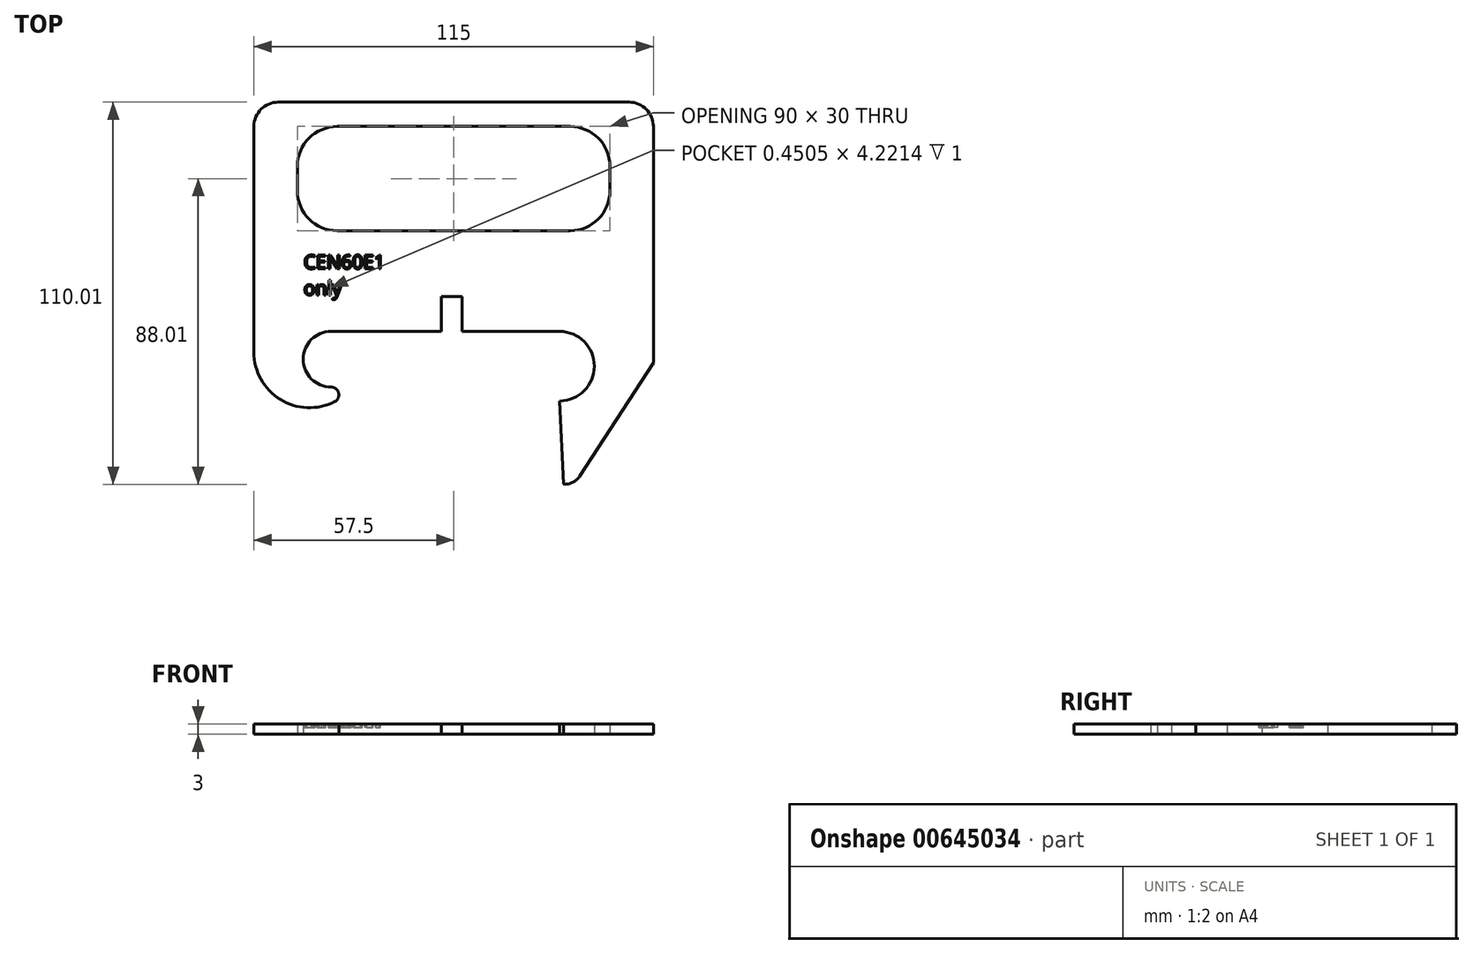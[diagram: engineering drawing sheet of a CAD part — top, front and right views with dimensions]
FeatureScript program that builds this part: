
annotation { "Feature Type Name" : "Feature", "Feature Type Description" : "" }
export const myFeature = defineFeature(function(context is Context, id is Id, definition is map)
    precondition{}
    {
        {
            var Q0;
            Q0=qCreatedBy(makeId("Top.planeOp"),FACE);
            var sketch = newSketch(context, id + "F0", { "sketchPlane" : qUnion([Q0])});
            skLineSegment(sketch, "E0.bottom", {"start": v(100.56, 114.07) * mm, "end": v(-100.56, 114.07) * mm, "construction": true});
            skLineSegment(sketch, "E0.top", {"start": v(100.56, -114.07) * mm, "end": v(-100.56, -114.07) * mm, "construction": true});
            skLineSegment(sketch, "E0.left", {"start": v(100.56, 114.07) * mm, "end": v(100.56, -114.07) * mm, "construction": true});
            skLineSegment(sketch, "E0.right", {"start": v(-100.56, 114.07) * mm, "end": v(-100.56, -114.07) * mm, "construction": true});
            skPoint(sketch, "E0.middle", {"position": v(0, 0) * mm});
            skLineSegment(sketch, "E1", {"start": v(0, 0) * mm, "end": v(-31.71, 0) * mm});
            skLineSegment(sketch, "E2", {"start": v(0, 0) * mm, "end": v(0, 10) * mm});
            skLineSegment(sketch, "E3", {"start": v(0, 10) * mm, "end": v(6, 10) * mm});
            skLineSegment(sketch, "E4", {"start": v(6, 10) * mm, "end": v(6, 0) * mm});
            skLineSegment(sketch, "E5", {"start": v(6, 0) * mm, "end": v(34.08, 0) * mm});
            skArc(sketch, "E6", {"start": v(34.08, -20) * mm, "mid": v(44.08, -10) * mm, "end": v(34.08, 0) * mm});
            skLineSegment(sketch, "E7", {"start": v(34.08, -20) * mm, "end": v(35.28, -44) * mm});
            skLineSegment(sketch, "E8", {"start": v(34.08, -20) * mm, "end": v(34.08, -27.07) * mm, "construction": true});
            skLineSegment(sketch, "E9", {"start": v(61.08, -9) * mm, "end": v(61.08, 59) * mm});
            skLineSegment(sketch, "E10", {"start": v(61.08, -9) * mm, "end": v(39.82, -41.74) * mm});
            skArc(sketch, "E11", {"start": v(39.82, -41.74) * mm, "mid": v(37.86, -43.49) * mm, "end": v(35.28, -44) * mm});
            skArc(sketch, "E12", {"start": v(-31.71, 0) * mm, "mid": v(-39.71, -8) * mm, "end": v(-31.71, -16) * mm});
            skArc(sketch, "E13", {"start": v(-30.7, -20.24) * mm, "mid": v(-29.53, -17.72) * mm, "end": v(-31.71, -16) * mm});
            skArc(sketch, "E14", {"start": v(-30.7, -20.24) * mm, "mid": v(-46.3, -19.6) * mm, "end": v(-53.92, -5.96) * mm});
            skLineSegment(sketch, "E15", {"start": v(-53.92, -5.96) * mm, "end": v(-53.92, 59) * mm});
            skLineSegment(sketch, "E16", {"start": v(54.08, 66) * mm, "end": v(-46.92, 66) * mm});
            skPoint(sketch, "E17.visualSharp", {"position": v(61.08, 66) * mm});
            skArc(sketch, "E17.filletArc", {"start": v(61.08, 59) * mm, "mid": v(59.03, 63.95) * mm, "end": v(54.08, 66) * mm});
            skPoint(sketch, "E18.visualSharp", {"position": v(-53.92, 66) * mm});
            skArc(sketch, "E18.filletArc", {"start": v(-46.92, 66) * mm, "mid": v(-51.87, 63.95) * mm, "end": v(-53.92, 59) * mm});
            skLineSegment(sketch, "E19.bottom", {"start": v(-29.94, 59) * mm, "end": v(37.1, 59) * mm});
            skLineSegment(sketch, "E19.top", {"start": v(-29.94, 29) * mm, "end": v(37.1, 29) * mm});
            skLineSegment(sketch, "E19.left", {"start": v(-41.42, 47.52) * mm, "end": v(-41.42, 40.48) * mm});
            skLineSegment(sketch, "E19.right", {"start": v(48.58, 47.52) * mm, "end": v(48.58, 40.48) * mm});
            skPoint(sketch, "E20.visualSharp", {"position": v(-41.42, 59) * mm});
            skArc(sketch, "E20.filletArc", {"start": v(-29.94, 59) * mm, "mid": v(-38.06, 55.64) * mm, "end": v(-41.42, 47.52) * mm});
            skPoint(sketch, "E21.visualSharp", {"position": v(-41.42, 29) * mm});
            skArc(sketch, "E21.filletArc", {"start": v(-41.42, 40.48) * mm, "mid": v(-38.06, 32.36) * mm, "end": v(-29.94, 29) * mm});
            skPoint(sketch, "E22.visualSharp", {"position": v(48.58, 29) * mm});
            skArc(sketch, "E22.filletArc", {"start": v(37.1, 29) * mm, "mid": v(45.22, 32.36) * mm, "end": v(48.58, 40.48) * mm});
            skPoint(sketch, "E23.visualSharp", {"position": v(48.58, 59) * mm});
            skArc(sketch, "E23.filletArc", {"start": v(48.58, 47.52) * mm, "mid": v(45.22, 55.64) * mm, "end": v(37.1, 59) * mm});
            skSolve(sketch);
        }
        {
            var Q0;
            Q0=makeQuery(id+"F0.imprint","IMPRINT",FACE,{"disambiguationData":[TD([[makeQuery(id+"F0.imprint","IMPRINT",EDGE,{"derivedFrom":sQuery(id+"F0.wireOp",EDGE,"E1")}),-1.0]])]});
            extrude(context, id + "F1", {"entities" : qUnion([Q0]), "depth" : 3 * mm, "offsetDistance" : 25 * mm});
        }
        {
            var Q0;
            Q0=makeQuery(id+"F1.opExtrude","CAP_FACE",FACE,{"disambiguationData":[OSD([sQuery(id+"F0.wireOp",EDGE,"E1"),sQuery(id+"F0.wireOp",EDGE,"E2"),sQuery(id+"F0.wireOp",EDGE,"E3"),sQuery(id+"F0.wireOp",EDGE,"E4"),sQuery(id+"F0.wireOp",EDGE,"E5"),sQuery(id+"F0.wireOp",EDGE,"E6"),sQuery(id+"F0.wireOp",EDGE,"E7"),sQuery(id+"F0.wireOp",EDGE,"E9"),sQuery(id+"F0.wireOp",EDGE,"E10"),sQuery(id+"F0.wireOp",EDGE,"E11"),sQuery(id+"F0.wireOp",EDGE,"E12"),sQuery(id+"F0.wireOp",EDGE,"E13"),sQuery(id+"F0.wireOp",EDGE,"E14"),sQuery(id+"F0.wireOp",EDGE,"E15"),sQuery(id+"F0.wireOp",EDGE,"E16"),sQuery(id+"F0.wireOp",EDGE,"E17.filletArc"),sQuery(id+"F0.wireOp",EDGE,"E18.filletArc"),sQuery(id+"F0.wireOp",EDGE,"E19.bottom"),sQuery(id+"F0.wireOp",EDGE,"E19.top"),sQuery(id+"F0.wireOp",EDGE,"E19.left"),sQuery(id+"F0.wireOp",EDGE,"E19.right"),sQuery(id+"F0.wireOp",EDGE,"E20.filletArc"),sQuery(id+"F0.wireOp",EDGE,"E21.filletArc"),sQuery(id+"F0.wireOp",EDGE,"E22.filletArc"),sQuery(id+"F0.wireOp",EDGE,"E23.filletArc")])],"isStart":false});
            var sketch = newSketch(context, id + "F2", { "sketchPlane" : qUnion([Q0])});
            skText(sketch, "E24", { "text": "CEN60E1\nonly", "fontName": "OpenSans-Regular.ttf"});
            const initialGuessF2  = {"E24": [-0.03959, 0.01802, 1, 0, 0.004]};
            skSetInitialGuess(sketch, initialGuessF2);
            skSolve(sketch);
        }
        {
            var Q0;
            Q0 = qSketchRegion(id + "F2", true);
            extrude(context, id + "F3", {"entities" : qUnion([Q0]), "operationType" : NewBodyOperationType.REMOVE, "oppositeDirection" : true, "depth" : 1 * mm, "offsetDistance" : 25 * mm});
        }
    });
